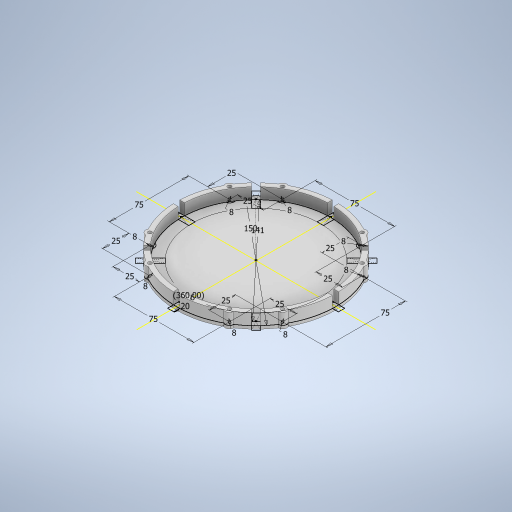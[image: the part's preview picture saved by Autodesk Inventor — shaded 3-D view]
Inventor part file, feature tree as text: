
AUTODESK INVENTOR PART (.ipt)
format: ipt  version: 2024.3 (Build 283343000, 343)  size: 353,280 bytes
history: native  units: in
note: dims shown in document units (in); Inventor stores cm internally (conversion verified against a paired STEP export)
features: extrude x2, sketch x1, hole x1
ambient origin geometry x8: Origin, YZ Plane, XZ Plane, XY Plane, X Axis, Y Axis, Z Axis, Center Point
bodies: Solid1 (feature_tree)
feature tree (4):
  sketch  "Sketch1"  dims[d0=5.5512in d1=5.9055in d4=0.2362in d5=0.7874in d6=3.1496in d8=360.0deg d12=0.1181in d13=0.0in d14=0.9843in d16=0.9843in d21=2.9528in d22=0.9843in d23=0.9843in d24=0.9843in d25=0.9843in d26=2.9528in d27=0.9843in d28=0.9843in d29=2.9528in d30=2.9528in d31=0.315in d32=0.315in d33=0.315in d34=0.315in d35=0.315in d36=0.315in d37=0.315in d38=0.315in d39=0.4134in d40=0.0in d41=0.1378in d42=0.2362in d43=0.1575in d44=0.0787in d45=90.0deg d46=0.315in d47=0.8108in]
  extrude  "Extrusion2"  Depth=0.1575in
  extrude  "Extrusion3"  Depth=0.2362in
  hole  "Hole1"  [1 undecoded]
note: 1 required parameter value undecoded (feature->parameter linkage not recoverable at this tier; creation-order binding heuristic only, values carry confidence <= 0.55)
